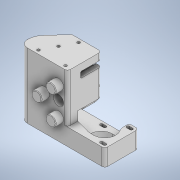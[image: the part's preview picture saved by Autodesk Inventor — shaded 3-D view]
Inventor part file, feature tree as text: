
AUTODESK INVENTOR PART (.ipt)
format: ipt  version: 2020.3 (Build 243373000, 373)  size: 530,432 bytes
history: native  units: mm
features: sketch x17, extrude x16, fillet x14, hole x1
ambient origin geometry x8: Origin, YZ Plane, XZ Plane, XY Plane, X Axis, Y Axis, Z Axis, Center Point
bodies: Solid1 (feature_tree)
feature tree (48):
  extrude  "Extrusion1"  Depth=66.0mm
  extrude  "Extrusion2"  Depth=2.0mm
  extrude  "Extrusion3"  Depth=2.0mm
  extrude  "Extrusion4"  Depth=56.0mm
  extrude  "Extrusion5"  Depth=38.8mm
  extrude  "Extrusion6"  Depth=4.45mm
  extrude  "Extrusion7"  Depth=4.45mm
  extrude  "Extrusion8"  Depth=5.0mm
  fillet  "Fillet1"  Radius=5.0mm
  fillet  "Fillet4"  Radius=5.0mm
  extrude  "Extrusion9"  Depth=86.0mm TaperAngle=0.0deg
  sketch  "Sketch12"  dims[d35=11.0mm d36=0.0mm d37=108.0mm d38=42.0mm d39=26.0mm]
  fillet  "Fillet9"  Radius=63.0mm
  fillet  "Fillet11"  Radius=74.0mm
  fillet  "Fillet12"  Radius=23.0mm
  fillet  "Fillet15"  Radius=14.0mm
  hole  "Hole2"  [1 undecoded]
  fillet  "Fillet18"  Radius=42.0mm
  fillet  "Fillet19"  Radius=26.0mm
  extrude  "Extrusion14"  Depth=18.0mm
  fillet  "Fillet20"  [1 undecoded]
  extrude  "Extrusion15"  Depth=8.0mm TaperAngle=0.0deg
  extrude  "Extrusion16"  Depth=5.0mm TaperAngle=0.0deg
  fillet  "Fillet21"  Radius=50.0mm
  extrude  "Extrusion17"  Depth=17.8mm
  fillet  "Fillet22"  Radius=1.0mm
  fillet  "Fillet23"  Radius=1.0mm
  extrude  "Extrusion18"  Depth=80.0mm
  extrude  "Extrusion20"  Depth=1.0mm
  extrude  "Extrusion21"  Depth=2.0mm
  fillet  "Fillet25"  Radius=40.0mm
  fillet  "Fillet26"  Radius=40.0mm
  sketch  "Sketch1"  dims[d2=108.0mm d3=0.0mm d6=66.0mm]
  sketch  "Sketch2"  dims[d7=86.0mm d8=0.0mm d9=2.0mm]
  sketch  "Sketch3"  dims[d10=2.0mm d11=2.0mm]
  sketch  "Sketch4"  dims[d12=2.0mm d13=56.0mm]
  sketch  "Sketch5"  dims[d14=56.0mm d15=38.8mm]
  sketch  "Sketch6"  dims[d16=4.45mm d17=4.45mm]
  sketch  "Sketch7"  dims[d18=4.45mm d19=4.45mm]
  sketch  "Sketch8"  dims[d20=5.0mm d21=5.0mm d22=5.0mm d23=5.0mm]
  sketch  "Sketch11"  dims[d24=38.8mm d25=5.0mm d26=5.0mm d27=5.0mm d28=5.0mm d29=86.0mm d30=0.0mm d31=63.0mm d32=74.0mm d33=23.0mm d34=14.0mm]
  sketch  "Sketch17"  dims[d40=55.0mm d41=18.0mm d42=0.0mm d43=0.0mm]
  sketch  "Sketch19"  dims[d44=28.0mm d45=8.0mm d46=0.0mm]
  sketch  "Sketch20"  dims[d48=5.0mm d49=5.0mm d50=0.0mm d51=50.0mm]
  sketch  "Sketch21"  dims[d52=17.8mm d53=17.8mm]
  sketch  "Sketch22"  dims[d54=17.8mm d55=14.0mm d56=0.0mm d57=1.0mm d60=1.0mm]
  sketch  "Sketch24"  dims[d62=30.0mm d63=80.0mm]
  sketch  "Sketch25"  dims[d64=38.0mm d65=0.0mm d92=1.0mm d94=2.0mm d104=40.0mm d105=40.0mm d108=5.0mm d119=5.0mm d120=10.0mm d121=24.0mm d122=24.0mm d123=24.0mm d125=5.0mm d126=6.0mm d127=4.0mm d128=2.0mm d129=90.0deg d130=36.0mm d131=20.594885mm d135=4.0mm d136=20.0mm d139=21.0mm d147=100.0mm d153=34.0mm d155=10.0mm d156=80.0mm d157=40.0mm d158=20.0mm d159=8.0mm d160=0.0mm d161=5.0mm d162=10.0mm d163=0.0mm d164=10.0mm d165=10.0mm d166=10.0mm d167=0.0mm d168=12.5mm d169=10.0mm d170=0.0mm d171=30.0mm d172=21.5mm d173=26.0mm d174=8.0mm d175=0.0mm d179=18.0mm d180=1.0mm d181=0.0mm d182=10.0mm d183=0.0mm d185=2.0mm d186=1.0mm d187=2.0mm d188=0.0mm d134=0.5mm d137=0.872665mm d184=0.5mm d189=0.5mm d190=0.872665mm d191=0.5mm d192=0.872665mm]
note: 2 required parameter values undecoded (feature->parameter linkage not recoverable at this tier; creation-order binding heuristic only, values carry confidence <= 0.55)
